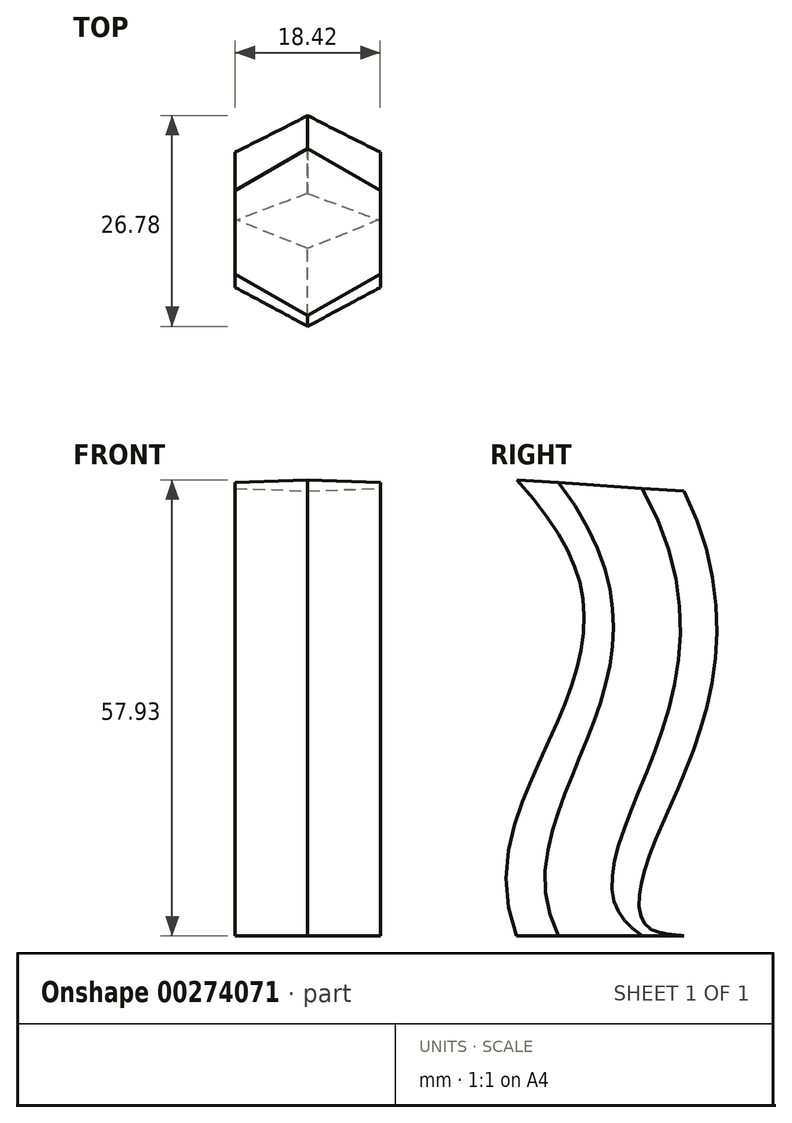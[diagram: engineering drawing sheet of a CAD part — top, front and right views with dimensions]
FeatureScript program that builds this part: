
annotation { "Feature Type Name" : "Feature", "Feature Type Description" : "" }
export const myFeature = defineFeature(function(context is Context, id is Id, definition is map)
    precondition{}
    {
        {
            var Q0;
            Q0=qCreatedBy(makeId("Right.planeOp"),FACE);
            var sketch = newSketch(context, id + "F0", { "sketchPlane" : qUnion([Q0])});
            skFitSpline(sketch, "E0", {"points": [v(0, 57.22) * mm, v(0, 0) * mm], "startDerivative": vector(51.4, -79.84) * mm, "endDerivative": vector(31.66, -42.6) * mm});
            skSolve(sketch);
        }
        {
            var Q0;
            Q0=qCreatedBy(makeId("Top.planeOp"),FACE);
            var sketch = newSketch(context, id + "F1", { "sketchPlane" : qUnion([Q0])});
            skCircle(sketch, "E1.cCircle", {"center": v(0, 0) * mm, "radius": 9.21 * mm, "construction": true});
            skLineSegment(sketch, "E1.0", {"start": v(-9.21, -5.32) * mm, "end": v(-9.21, 5.32) * mm});
            skLineSegment(sketch, "E1.1", {"start": v(-9.21, 5.32) * mm, "end": v(0, 10.64) * mm});
            skLineSegment(sketch, "E1.2", {"start": v(0, 10.64) * mm, "end": v(9.21, 5.32) * mm});
            skLineSegment(sketch, "E1.3", {"start": v(9.21, 5.32) * mm, "end": v(9.21, -5.32) * mm});
            skLineSegment(sketch, "E1.4", {"start": v(9.21, -5.32) * mm, "end": v(0, -10.64) * mm});
            skLineSegment(sketch, "E1.5", {"start": v(0, -10.64) * mm, "end": v(-9.21, -5.32) * mm});
            skPoint(sketch, "E1.0.midPoint", {"position": v(-9.21, 0) * mm});
            skSolve(sketch);
        }
        {
            var Q0;
            Q0=makeQuery(id+"F1.imprint","IMPRINT",FACE,{"disambiguationData":[TD([[makeQuery(id+"F1.imprint","IMPRINT",EDGE,{"derivedFrom":sQuery(id+"F1.wireOp",EDGE,"E1.0")}),-1.0]])]});
            var Q1;
            Q1=sQuery(id+"F0.wireOp",EDGE,"E0");
            sweep(context, id + "F2", {"profiles" : qUnion([Q0]), "path" : qUnion([Q1])});
        }
    });
